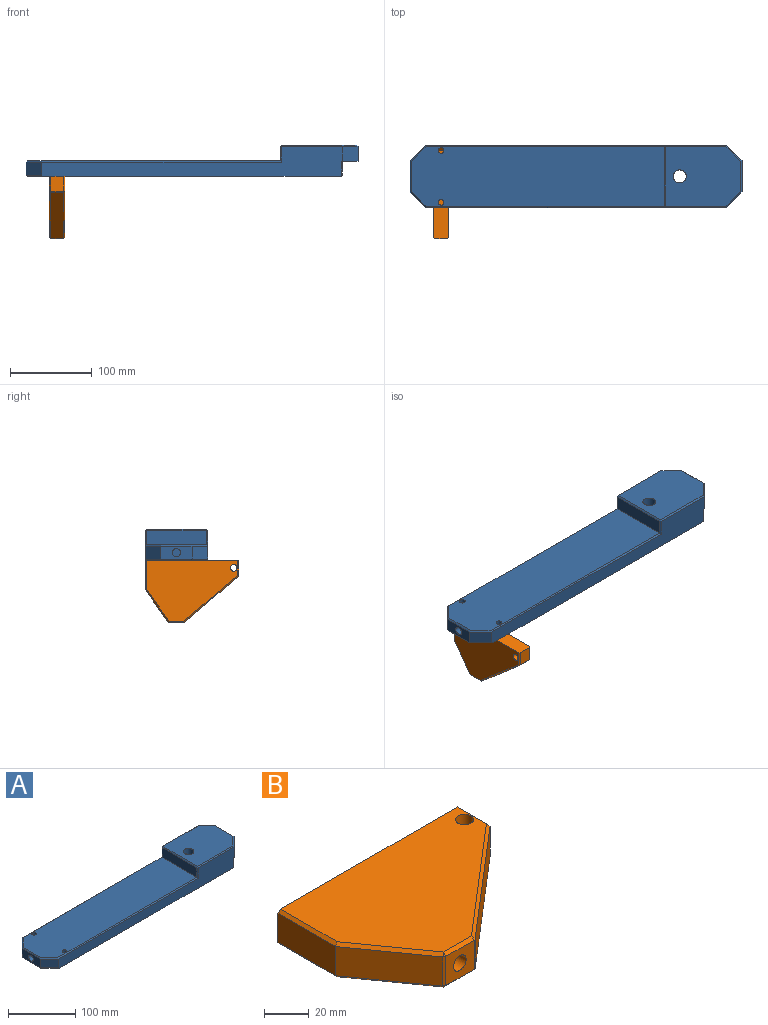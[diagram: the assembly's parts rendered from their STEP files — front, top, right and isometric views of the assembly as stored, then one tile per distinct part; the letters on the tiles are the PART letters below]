
ASSEMBLY  parts=2 mates=1
PART A: 45 faces, bbox 406.4x76.2x38.1 mm
  f0: plane 38.1x18.21mm, normal (1,0,0), area 615.1mm2, adj f1,f2,f15,f23,f42
  f1: plane 19.05x19.05mm, normal (0.71,-0.71,0), area 490.6mm2, adj f0,f6,f15,f27
  f2: plane 19.05x19.05mm, normal (0.71,0.71,0), area 490.6mm2, adj f0,f4,f15,f19
  f3: plane 384.18x76.2mm, normal (0,0,-1), area 28610.6mm2, adj f4,f6,f7,f13,f14,f17,f18,f20
  f4: plane 367.64x36.51mm, normal (0,1,0), area 7781.1mm2, adj f2,f3,f15,f20,f21,f22,f24,f25
  f5: plane 73.03x17.46mm, normal (-1,0,0), area 1275.2mm2, adj f9,f21,f29,f34
  f6: plane 368.3x36.51mm, normal (0,-1,0), area 7823.4mm2, adj f1,f3,f12,f15,f17,f30,f34,f36
  f7: cylinder r=7.94mm len=38.1mm, axis (0,0,-1), area 1867.7mm2, adj f3,f8,f44
  f8: plane 92.15x73.03mm, normal (0,0,1), area 6202.8mm2, adj f7,f19,f22,f23,f27,f29,f30
  f9: plane 309.49x73.03mm, normal (0,0,1), area 22194.9mm2, adj f5,f13,f14,f25,f31,f33,f35,f36
  f10: plane 18.59x18.59mm, normal (-0.71,0.71,0), area 417.2mm2, adj f11,f20,f24,f31
  f11: plane 38.1x15.88mm, normal (-1,0,0), area 526.2mm2, adj f10,f12,f18,f33,f40
  f12: plane 19.05x19.05mm, normal (-0.71,-0.71,0), area 427.7mm2, adj f6,f11,f17,f35
  f13: cylinder r=3.51mm len=19.05mm, axis (0,0,-1), area 419.6mm2, adj f3,f9
  f14: cylinder r=3.51mm len=19.05mm, axis (0,0,-1), area 419.6mm2, adj f3,f9
  f15: plane 76.2x20.64mm, normal (0,0,-1), area 1091.2mm2, adj f0,f1,f2,f4,f6,f16,f37,f39
  f16: plane 73.03x16.72mm, normal (1,0,0), area 1220.7mm2, adj f15,f37,f38,f39
  f17: plane 21.3x19.71mm, normal (-0.5,-0.5,-0.71), area 61.5mm2, adj f3,f6,f12,f18
  f18: plane 38.1x1.59mm, normal (-0.71,0,-0.71), area 84.1mm2, adj f3,f11,f17,f20
  f19: plane 19.71x19.71mm, normal (0.5,0.5,0.71), area 59mm2, adj f2,f8,f22,f23
  f20: plane 21.3x19.71mm, normal (-0.5,0.5,-0.71), area 61.3mm2, adj f3,f4,f10,f18,f24
  f21: plane 19.05x1.59mm, normal (-0.71,0.71,0), area 41mm2, adj f4,f5,f25,f26
  f22: plane 74.69x1.59mm, normal (0,0.71,0.71), area 166.9mm2, adj f4,f8,f19,f26
  f23: plane 38.1x1.59mm, normal (0.71,0,0.71), area 84.1mm2, adj f0,f8,f19,f27
  f24: plane 16.34x1.12mm, normal (-0.38,0.92,0), area 19.6mm2, adj f4,f10,f20,f28
  f25: plane 292.96x1.59mm, normal (0,0.71,0.71), area 655.9mm2, adj f4,f9,f21,f28
  f26: plane 1.59x1.59mm, normal (-0.58,0.58,0.58), area 2.2mm2, adj f21,f22,f29
  f27: plane 19.71x19.71mm, normal (0.5,-0.5,0.71), area 59mm2, adj f1,f8,f23,f30
  f28: plane 1.59x1.59mm, normal (-0.28,0.68,0.68), area 1.3mm2, adj f24,f25,f31
  f29: plane 73.03x1.59mm, normal (-0.71,0,0.71), area 163.9mm2, adj f5,f8,f26,f32
  f30: plane 74.69x1.59mm, normal (0,-0.71,0.71), area 166.9mm2, adj f6,f8,f27,f32
  f31: plane 19.71x19.24mm, normal (-0.5,0.5,0.71), area 58.3mm2, adj f9,f10,f28,f33
  f32: plane 1.59x1.59mm, normal (-0.58,-0.58,0.58), area 2.2mm2, adj f29,f30,f34
  f33: plane 38.1x1.59mm, normal (-0.71,0,0.71), area 84.1mm2, adj f9,f11,f31,f35
  f34: plane 19.05x1.59mm, normal (-0.71,-0.71,0), area 41mm2, adj f5,f6,f32,f36
  f35: plane 19.71x19.71mm, normal (-0.5,-0.5,0.71), area 59mm2, adj f9,f12,f33,f36
  f36: plane 293.61x1.59mm, normal (0,-0.71,0.71), area 656.7mm2, adj f6,f9,f34,f35
  f37: plane 18.3x1.59mm, normal (0.71,-0.71,0), area 39.3mm2, adj f6,f15,f16,f38
  f38: plane 76.2x1.59mm, normal (0.71,0,-0.71), area 167.5mm2, adj f3,f16,f37,f39
  f39: plane 18.3x1.59mm, normal (0.71,0.71,0), area 39.3mm2, adj f4,f15,f16,f38
  f40: cylinder r=5mm len=38.1mm, axis (-1,0,0), area 1197.9mm2, adj f11,f41
  f41: plane 10.01x10.01mm, normal (-1,0,0), area 78.7mm2, adj f40
  f42: cylinder r=5mm len=38.1mm, axis (1,0,0), area 1197.9mm2, adj f0,f43
  f43: plane 10.01x10.01mm, normal (1,0,0), area 78.7mm2, adj f42
  f44: cylinder r=3.17mm len=30.85mm, axis (0,1,0), area 608.3mm2, adj f4,f7
PART B: 35 faces, bbox 114.3x76.2x19.1 mm
  f0: plane 18.32x15.88mm, normal (1,0,0), area 290.8mm2, adj f1,f18,f19,f20
  f1: plane 114.3x19.05mm, normal (0,1,0), area 2071.8mm2, adj f0,f2,f5,f6,f9,f11,f15,f16
  f2: plane 36.1x15.88mm, normal (-1,0,0), area 573.1mm2, adj f1,f14,f15,f16
  f3: plane 17.64x15.88mm, normal (0,-1,0), area 229.8mm2, adj f7,f22,f27,f30,f33
  f4: plane 65.67x56.29mm, normal (0.65,-0.76,0), area 1373.2mm2, adj f19,f28,f29,f33
  f5: plane 111.13x74.61mm, normal (0,0,1), area 5850.1mm2, adj f1,f15,f17,f18,f27,f28,f34
  f6: plane 111.13x74.61mm, normal (0,0,-1), area 5850.1mm2, adj f1,f16,f20,f21,f29,f30,f34
  f7: cylinder r=4mm len=38.1mm, axis (0,-1,0), area 957.6mm2, adj f3,f8
  f8: plane 8x8mm, normal (0,-1,0), area 50.3mm2, adj f7
  f9: cylinder r=4mm len=31.75mm, axis (0,1,0), area 734mm2, adj f1,f10,f13
  f10: plane 8x4mm, normal (0,1,0), area 25.1mm2, adj f9,f13
  f11: cylinder r=4mm len=31.75mm, axis (0,1,0), area 798mm2, adj f1,f12
  f12: plane 8x8mm, normal (0,1,0), area 50.3mm2, adj f11
  f13: plane 8x8mm, normal (0.89,0.45,0), area 56.2mm2, adj f9,f10
  f14: plane 39.43x28.1mm, normal (-0.81,-0.58,0), area 768.7mm2, adj f2,f17,f21,f22
  f15: plane 36.1x1.59mm, normal (-0.71,0,0.71), area 80.5mm2, adj f1,f2,f5,f17
  f16: plane 36.1x1.59mm, normal (-0.71,0,-0.71), area 80.5mm2, adj f1,f2,f6,f21
  f17: plane 39.94x29.39mm, normal (-0.58,-0.41,0.71), area 108.1mm2, adj f5,f14,f15,f23
  f18: plane 18.32x1.59mm, normal (0.71,0,0.71), area 41.1mm2, adj f0,f1,f5,f24
  f19: plane 15.88x1.21mm, normal (0.91,-0.42,0), area 21.1mm2, adj f0,f4,f24,f25
  f20: plane 18.32x1.59mm, normal (0.71,0,-0.71), area 41.1mm2, adj f0,f1,f6,f25
  f21: plane 39.94x29.39mm, normal (-0.58,-0.41,-0.71), area 108.1mm2, adj f6,f14,f16,f26
  f22: plane 15.88x1.29mm, normal (-0.46,-0.89,0), area 23.1mm2, adj f3,f14,f23,f26
  f23: plane 1.59x1.59mm, normal (-0.34,-0.66,0.66), area 1.5mm2, adj f17,f22,f27
  f24: plane 1.59x1.59mm, normal (0.67,-0.31,0.67), area 1.4mm2, adj f18,f19,f28
  f25: plane 1.59x1.59mm, normal (0.67,-0.31,-0.67), area 1.4mm2, adj f19,f20,f29
  f26: plane 1.59x1.59mm, normal (-0.34,-0.66,-0.66), area 1.5mm2, adj f21,f22,f30
  f27: plane 17.64x1.59mm, normal (0,-0.71,0.71), area 39.6mm2, adj f3,f5,f23,f31
  f28: plane 66.71x57.5mm, normal (0.46,-0.54,0.71), area 194.2mm2, adj f4,f5,f24,f31
  f29: plane 66.71x57.5mm, normal (0.46,-0.54,-0.71), area 194.2mm2, adj f4,f6,f25,f32
  f30: plane 17.64x1.59mm, normal (0,-0.71,-0.71), area 39.6mm2, adj f3,f6,f26,f32
  f31: plane 1.59x1.59mm, normal (0.25,-0.68,0.68), area 1.2mm2, adj f27,f28,f33
  f32: plane 1.59x1.59mm, normal (0.25,-0.68,-0.68), area 1.2mm2, adj f29,f30,f33
  f33: plane 15.88x1.03mm, normal (0.35,-0.94,0), area 17.5mm2, adj f3,f4,f31,f32
  f34: cylinder r=4mm len=19.05mm, axis (0,0,1), area 478.8mm2, adj f5,f6
PLACE A t=(-58.37,186.9,-35.93)mm
PLACE B rot(axis=(0.58,-0.58,-0.58),120deg) t=(-50.3,40.07,-108.28)mm
MATE fastened B.f9 <-> A.f13  axis (0,0,1) through (-59.82,81.28,-35.93)mm
